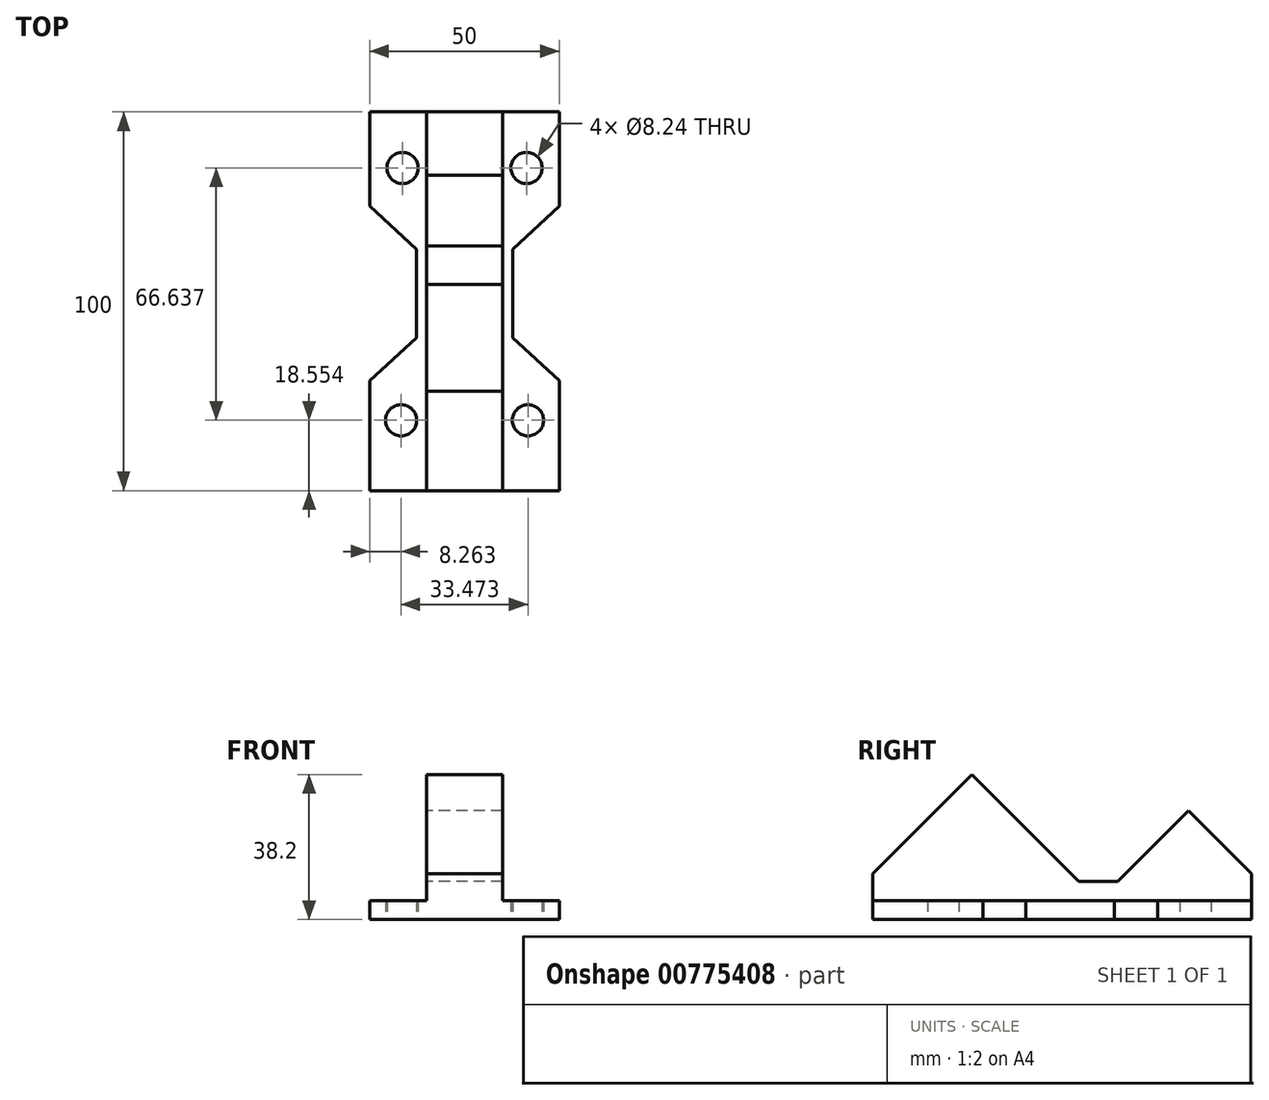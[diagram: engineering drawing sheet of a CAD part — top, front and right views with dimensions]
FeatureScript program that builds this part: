
annotation { "Feature Type Name" : "Feature", "Feature Type Description" : "" }
export const myFeature = defineFeature(function(context is Context, id is Id, definition is map)
    precondition{}
    {
        {
            var Q0;
            Q0=qCreatedBy(makeId("Top.planeOp"),FACE);
            var sketch = newSketch(context, id + "F0", { "sketchPlane" : qUnion([Q0])});
            skLineSegment(sketch, "E0.bottom", {"start": v(-25, 57.63) * mm, "end": v(2.5, 57.63) * mm});
            skLineSegment(sketch, "E0.top", {"start": v(-25, -42.37) * mm, "end": v(2.5, -42.37) * mm});
            skLineSegment(sketch, "E0.left", {"start": v(-25, 57.63) * mm, "end": v(-25, 32.82) * mm});
            skPoint(sketch, "E0.middle", {"position": v(0, 0) * mm});
            skLineSegment(sketch, "E1", {"start": v(2.5, 57.63) * mm, "end": v(2.5, -42.37) * mm});
            skCircle(sketch, "E2", {"center": v(-16.36, 42.82) * mm, "radius": 4.12 * mm});
            skCircle(sketch, "E3", {"center": v(-16.74, -23.82) * mm, "radius": 4.12 * mm});
            skLineSegment(sketch, "E4", {"start": v(-25, 32.82) * mm, "end": v(-12.68, 21.38) * mm});
            skLineSegment(sketch, "E5", {"start": v(-12.68, 21.38) * mm, "end": v(-12.68, -1.98) * mm});
            skLineSegment(sketch, "E6", {"start": v(-12.68, -1.98) * mm, "end": v(-25, -13.3) * mm});
            skLineSegment(sketch, "E7.trimOffspring", {"start": v(-25, -13.3) * mm, "end": v(-25, -42.37) * mm});
            skSolve(sketch);
        }
        {
            var Q0;
            Q0=makeQuery(id+"F0.imprint","IMPRINT",FACE,{"disambiguationData":[TD([[makeQuery(id+"F0.imprint","IMPRINT",EDGE,{"derivedFrom":sQuery(id+"F0.wireOp",EDGE,"E0.bottom")}),-1.0]])]});
            extrude(context, id + "F1", {"entities" : qUnion([Q0]), "depth" : 5 * mm, "offsetDistance" : 25 * mm});
        }
        {
            var Q0;
            Q0=makeQuery(id+"F1.opExtrude","CAP_FACE",FACE,{"disambiguationData":[OSD([sQuery(id+"F0.wireOp",EDGE,"E0.bottom"),sQuery(id+"F0.wireOp",EDGE,"E0.top"),sQuery(id+"F0.wireOp",EDGE,"E0.left"),sQuery(id+"F0.wireOp",EDGE,"E1")])],"isStart":false});
            var sketch = newSketch(context, id + "F2", { "sketchPlane" : qUnion([Q0])});
            skLineSegment(sketch, "E8.bottom", {"start": v(2.5, 57.63) * mm, "end": v(-10, 57.63) * mm});
            skLineSegment(sketch, "E8.top", {"start": v(2.5, -42.37) * mm, "end": v(-10, -42.37) * mm});
            skLineSegment(sketch, "E8.left", {"start": v(2.5, 57.63) * mm, "end": v(2.5, -42.37) * mm});
            skLineSegment(sketch, "E8.right", {"start": v(-10, 57.63) * mm, "end": v(-10, -42.37) * mm});
            skSolve(sketch);
        }
        {
            var Q0;
            Q0=makeQuery(id+"F2.imprint","IMPRINT",FACE,{"disambiguationData":[TD([[makeQuery(id+"F2.imprint","IMPRINT",EDGE,{"derivedFrom":sQuery(id+"F2.wireOp",EDGE,"E8.bottom")}),-1.0]])]});
            extrude(context, id + "F3", {"entities" : qUnion([Q0]), "operationType" : NewBodyOperationType.ADD, "endBound" : BoundingType.THROUGH_ALL, "depth" : 25 * mm, "offsetDistance" : 25 * mm});
        }
        {
            var Q0;
            Q0=makeQuery(id+"F3.opExtrude","SWEPT_FACE",FACE,{"disambiguationData":[OSD([sQuery(id+"F2.wireOp",EDGE,"E8.right")])]});
            var sketch = newSketch(context, id + "F4", { "sketchPlane" : qUnion([Q0])});
            skLineSegment(sketch, "E9", {"start": v(-57.63, 5) * mm, "end": v(-57.63, 12) * mm});
            skLineSegment(sketch, "E10", {"start": v(-57.63, 12) * mm, "end": v(-40.93, 28.7) * mm});
            skLineSegment(sketch, "E11", {"start": v(-40.93, 28.7) * mm, "end": v(-22.23, 10) * mm});
            skLineSegment(sketch, "E12", {"start": v(-22.23, 10) * mm, "end": v(-12.04, 10) * mm});
            skLineSegment(sketch, "E13", {"start": v(-12.04, 10) * mm, "end": v(16.16, 38.2) * mm});
            skLineSegment(sketch, "E14", {"start": v(16.16, 38.2) * mm, "end": v(42.37, 12) * mm});
            skLineSegment(sketch, "E15", {"start": v(42.37, 12) * mm, "end": v(42.37, 5) * mm});
            skLineSegment(sketch, "E16", {"start": v(42.37, 5) * mm, "end": v(-57.63, 5) * mm});
            skSolve(sketch);
        }
        {
            var Q0;
            {var subQ0=sQuery(id+"F4.wireOp",EDGE,"E10");Q0=makeQuery(id+"F4.imprint","IMPRINT",FACE,{"disambiguationData":[TD([[makeQuery(id+"F4.imprint","IMPRINT",EDGE,{"derivedFrom":subQ0}),1.0]])]});}
            extrude(context, id + "F5", {"entities" : qUnion([Q0]), "operationType" : NewBodyOperationType.REMOVE, "endBound" : BoundingType.THROUGH_ALL, "oppositeDirection" : true, "depth" : 25 * mm, "offsetDistance" : 25 * mm});
        }
        {
            var Q0;
            Q0=makeQuery(id+"F1.opExtrude","SWEPT_BODY",BODY,{"disambiguationData":[OSD([sQuery(id+"F0.wireOp",EDGE,"E0.bottom"),sQuery(id+"F0.wireOp",EDGE,"E0.top"),sQuery(id+"F0.wireOp",EDGE,"E0.left"),sQuery(id+"F0.wireOp",EDGE,"E1")])]});
            var Q1;
            Q1=qCreatedBy(makeId("Right.planeOp"),FACE);
            mirror(context, id + "F6", {"operationType" : NewBodyOperationType.ADD, "entities" : qUnion([Q0]), "mirrorPlane" : qUnion([Q1])});
        }
    });
